# Revit family: Storage-Teknion-EMC2_Low_Double_Cabinet-R2016
name_source: partatom
category: Furniture
revit_build: Autodesk Revit 2018 (Build: 20190510_1515(x64)
units: mm (PartAtom-declared; Revit-internal decimal feet)

## family parameters
Always vertical = Yes
Cut with Voids When Loaded = No
OmniClass Number = 23.40.20.00
OmniClass Title = General Furniture and Specialties
Room Calculation Point = No
Shared = Yes
Work Plane-Based = No

## types (4) — shared parameters
Assembly Code = E2020200
Manufacturer = Teknion
Manufacturer Fax = 416.661.4586
Part Number = EMC2
Product Documentation Link = https://assets.teknion.com
Product Line = Emote
Product Page URL = https://www.teknion.com
Series = Emote
Sustainability Data = https://www.teknion.com
URL = www.teknion.com
Unit Weight URL = http://www.teknion.com
Warranty = http://www.teknion.com

## per-type parameters (varying)
| type | Description | Left Double Doors | Left Full Height Drawer | Left Open | Left Partial Height Drawer | Left Single Door | Model |
| Left Open Drawer Configuration | Low Double Cabinet, Left Open Drawer Configuration , 57" Width | No | No | Yes | No | No | EMC2OP__57 |
| Left Double Doors Drawer Configuration | Low Double Cabinet, Left Double Doors Drawer Configuration , 57" Width | Yes | No | No | No | No | EMC2CL__57 |
| Left Partial Height Drawer Configuration | Low Double Cabinet, Left Partial Height Drawer Configuration , 57" Width | No | No | No | Yes | Yes | EMC2PD__57 |
| Left Full Height Drawer Configuration | Low Double Cabinet, Left Full Height Drawer Configuration , 57" Width | No | Yes | No | No | Yes | EMC2FD__57 |

## geometry (parser evidence)
native form markers: Blend x43, Sweep x2
no freeform markers — native parametric forms only
